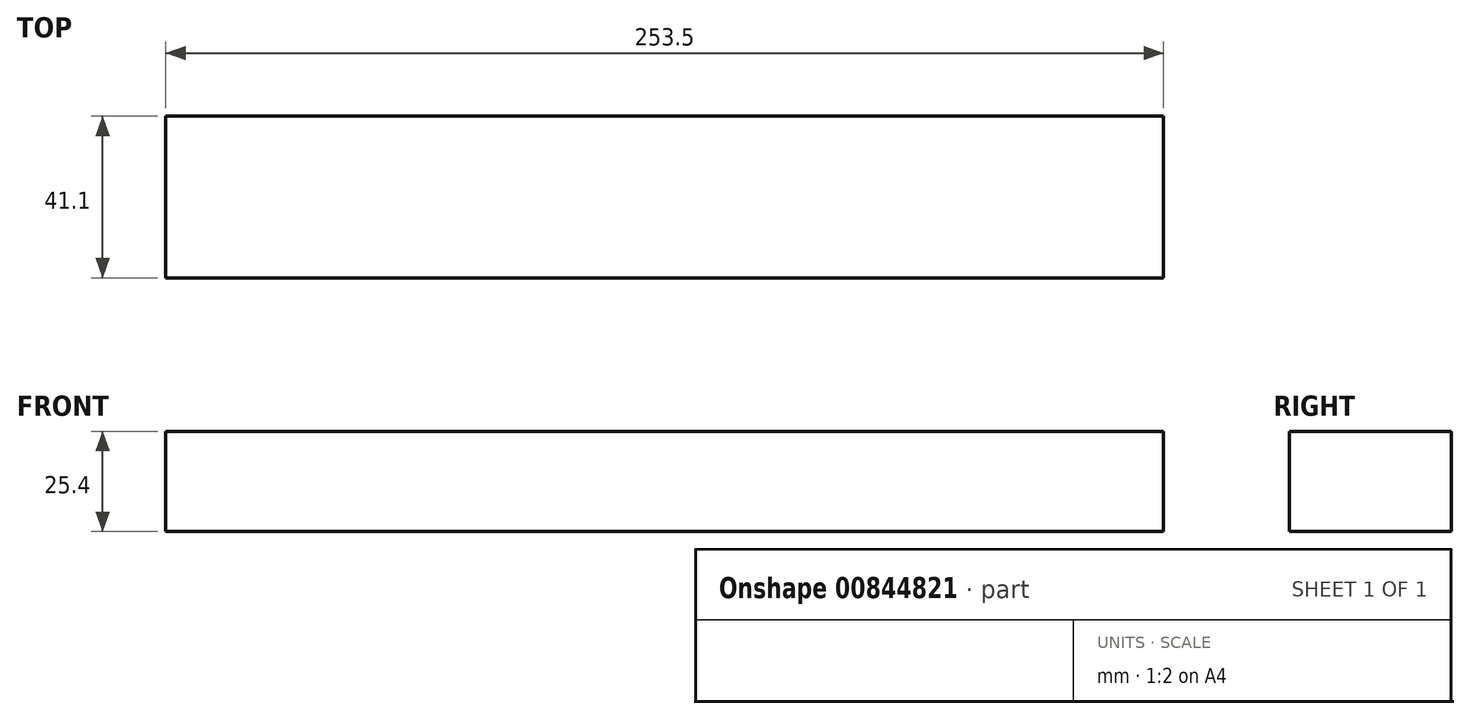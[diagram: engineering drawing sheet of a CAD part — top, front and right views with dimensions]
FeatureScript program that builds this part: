
annotation { "Feature Type Name" : "Feature", "Feature Type Description" : "" }
export const myFeature = defineFeature(function(context is Context, id is Id, definition is map)
    precondition{}
    {
        {
            var Q0;
            Q0=qCreatedBy(makeId("Top.planeOp"),FACE);
            var sketch = newSketch(context, id + "F0", { "sketchPlane" : qUnion([Q0])});
            skLineSegment(sketch, "E0.bottom", {"start": v(-126.75, -20.55) * mm, "end": v(126.75, -20.55) * mm});
            skLineSegment(sketch, "E0.top", {"start": v(-126.75, 20.55) * mm, "end": v(126.75, 20.55) * mm});
            skLineSegment(sketch, "E0.left", {"start": v(-126.75, -20.55) * mm, "end": v(-126.75, 20.55) * mm});
            skLineSegment(sketch, "E0.right", {"start": v(126.75, -20.55) * mm, "end": v(126.75, 20.55) * mm});
            skPoint(sketch, "E0.middle", {"position": v(0, 0) * mm});
            skSolve(sketch);
        }
        {
            var Q0;
            Q0=sQuery(id+"F0.wireOp",EDGE,"E0.right");
            var Q1;
            Q1=sQuery(id+"F0.wireOp",EDGE,"E0.left");
            var Q2;
            Q2=sQuery(id+"F0.wireOp",EDGE,"E0.bottom");
            var Q3;
            Q3=sQuery(id+"F0.wireOp",EDGE,"E0.top");
            extrude(context, id + "F1", {"bodyType" : ToolBodyType.SURFACE, "surfaceEntities" : qUnion([Q0, Q1, Q2, Q3]), "depth" : 25.4 * mm, "offsetDistance" : 25.4 * mm});
        }
    });
